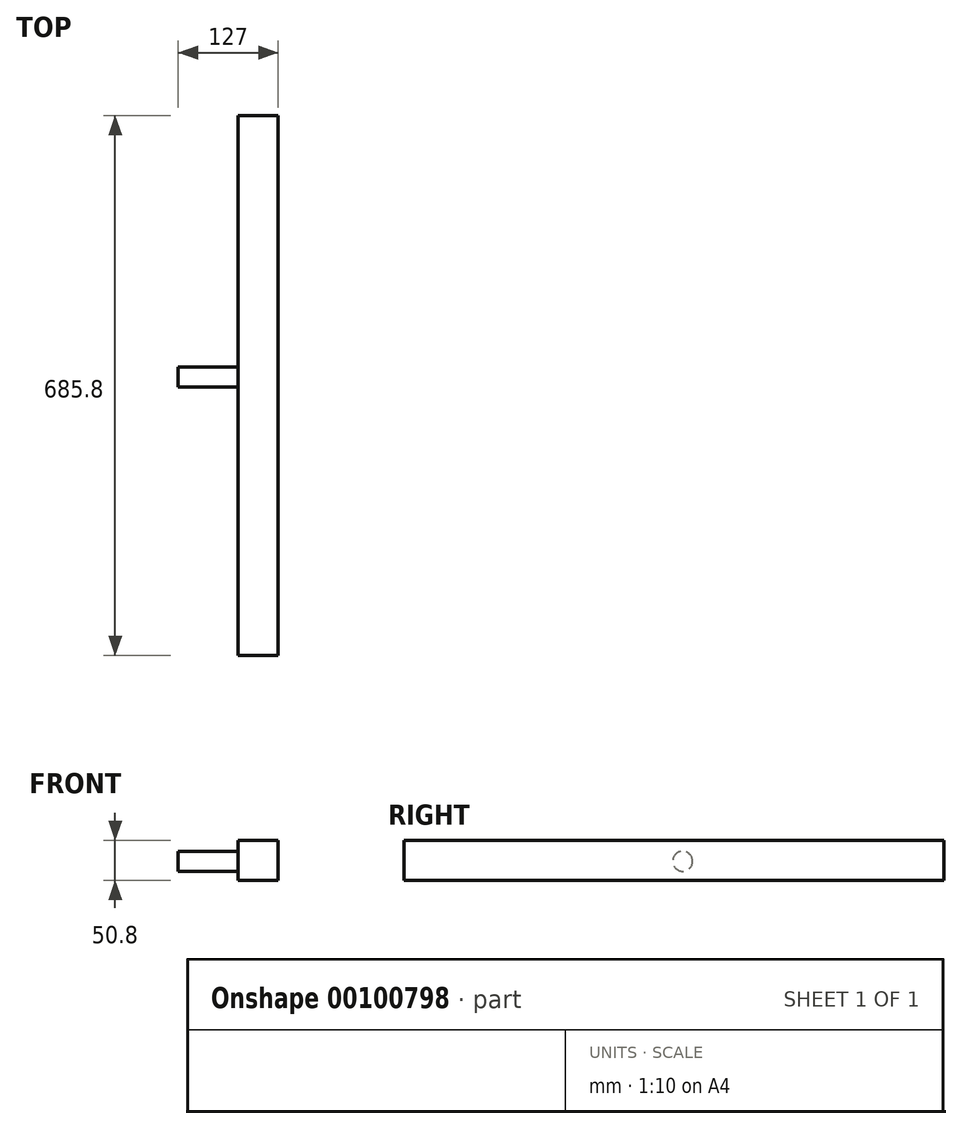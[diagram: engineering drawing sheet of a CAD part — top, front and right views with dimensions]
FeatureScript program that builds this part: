
annotation { "Feature Type Name" : "Feature", "Feature Type Description" : "" }
export const myFeature = defineFeature(function(context is Context, id is Id, definition is map)
    precondition{}
    {
        {
            var Q0;
            Q0=qCreatedBy(makeId("Front.planeOp"),FACE);
            var sketch = newSketch(context, id + "F0", { "sketchPlane" : qUnion([Q0])});
            skLineSegment(sketch, "E0.bottom", {"start": v(0, 0) * mm, "end": v(50.8, 0) * mm});
            skLineSegment(sketch, "E0.top", {"start": v(0, 50.8) * mm, "end": v(50.8, 50.8) * mm});
            skLineSegment(sketch, "E0.left", {"start": v(0, 0) * mm, "end": v(0, 50.8) * mm});
            skLineSegment(sketch, "E0.right", {"start": v(50.8, 0) * mm, "end": v(50.8, 50.8) * mm});
            skSolve(sketch);
        }
        {
            var Q0;
            Q0 = qSketchRegion(id + "F0", true);
            extrude(context, id + "F1", {"entities" : qUnion([Q0]), "depth" : 685.8 * mm});
        }
        {
            var Q0;
            Q0=makeQuery(id+"F1.opExtrude","SWEPT_FACE",FACE,{"disambiguationData":[OSD([sQuery(id+"F0.wireOp",EDGE,"E0.left")])]});
            var sketch = newSketch(context, id + "F2", { "sketchPlane" : qUnion([Q0])});
            skCircle(sketch, "E1", {"center": v(332.07, 24.25) * mm, "radius": 12.7 * mm});
            skSolve(sketch);
        }
        {
            var Q0;
            Q0 = qSketchRegion(id + "F2", true);
            extrude(context, id + "F3", {"entities" : qUnion([Q0]), "operationType" : NewBodyOperationType.ADD, "depth" : 76.2 * mm});
        }
    });
